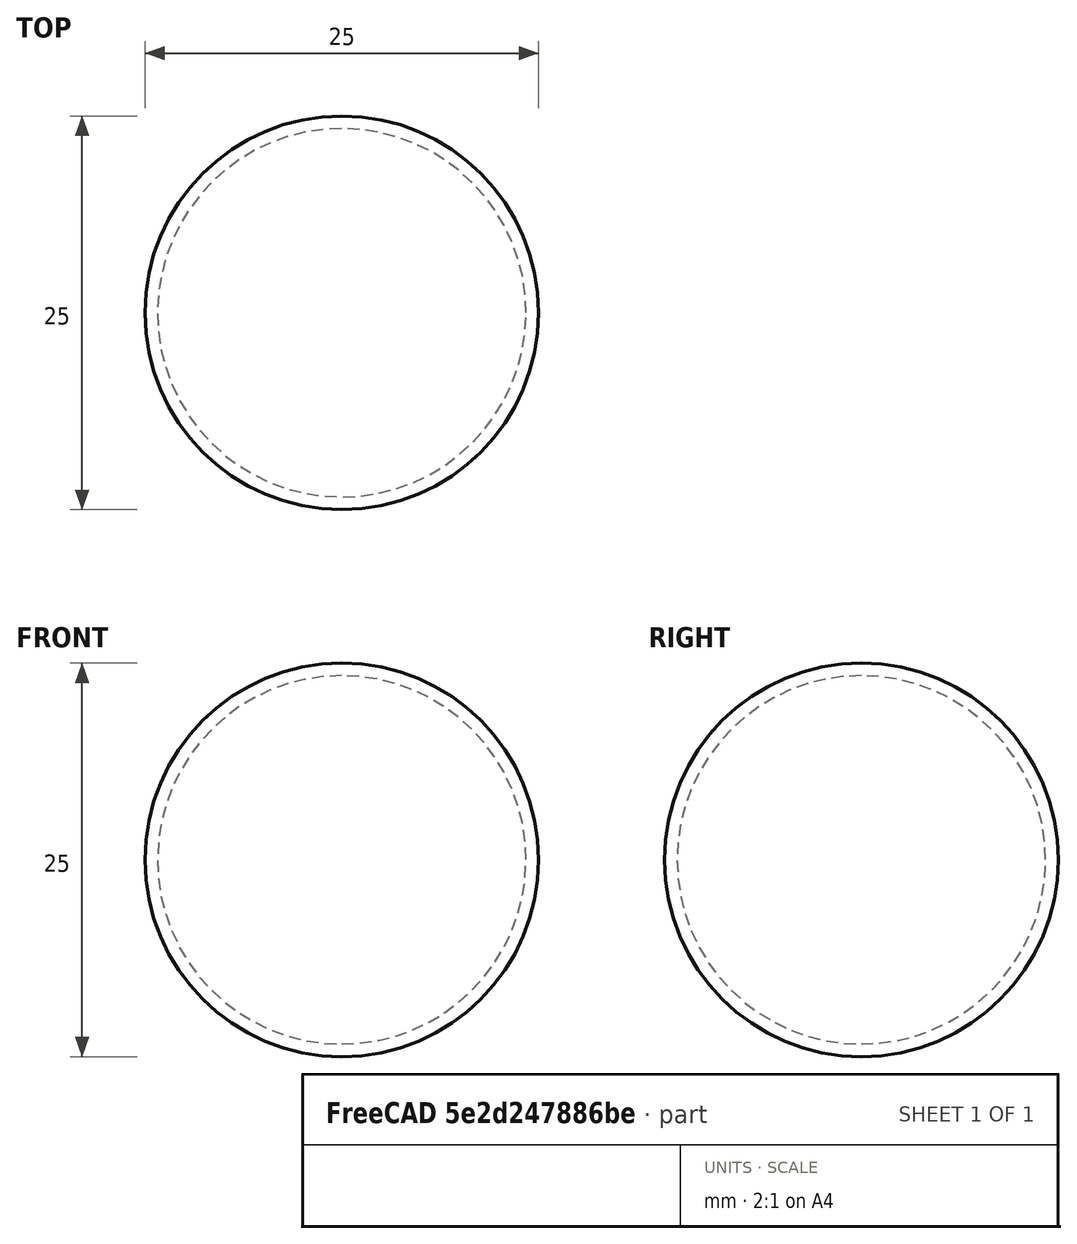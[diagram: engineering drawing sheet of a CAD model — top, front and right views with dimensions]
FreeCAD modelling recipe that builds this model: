
FCSTD DOCUMENT  (FreeCAD 2021.1015R24301 +3962 (Git))
Label: sphere
License: All rights reserved
LicenseURL: http://en.wikipedia.org/wiki/All_rights_reserved
objects: Sketcher::SketchObject×1, PartDesign::Revolution×1, PartDesign::Body×1, Mesh::Feature×1
note: 5 computed .brp shape members not serialized (recipe doc carries the construction recipe); baked Part::Feature solids carry a one-line shape summary decoded from their .brp

FEATURE [Sketcher::SketchObject] Sketch
  FullyConstrained = true
  MapMode = 5
  Placement = pos=(0,0,0) rot=(1,0,0;1.5708rad)
  Support = -> [XZ_Plane]
  sketch-geometry (4):
    g0: ArcOfCircle CenterX=0 CenterY=12.5 CenterZ=0 NormalX=0 NormalY=0 NormalZ=1 AngleXU=0 Radius=12.5 StartAngle=4.71239 EndAngle=7.85398
    g1: ArcOfCircle CenterX=0 CenterY=12.5 CenterZ=0 NormalX=0 NormalY=0 NormalZ=1 AngleXU=0 Radius=11.7 StartAngle=4.71239 EndAngle=7.85398
    g2: LineSegment StartX=-2.3e-15 StartY=0 StartZ=0 EndX=-2.3e-15 EndY=0.8 EndZ=0
    g3: LineSegment StartX=0 StartY=24.2 StartZ=0 EndX=0 EndY=25 EndZ=0
  constraints (12):
    c: PointOnObject(g0,g-2)
    c: Coincident(g0,g-1)
    c: PointOnObject(g0,g-2)
    c: Coincident(g1,g0)
    c: Coincident(g2,g0)
    c: Coincident(g2,g1)
    c: Coincident(g3,g1)
    c: Coincident(g3,g0)
    c: Vertical(g2)
    c: Vertical(g3)
    c: Diameter(g0) = 25
    c: DistanceY(g2,g2) = 0.8
FEATURE [PartDesign::Revolution] Revolution
  Angle = 360
  Axis = (0,2e-16,1)
  Base = (0,0,0)
  ClaimChildren = false
  Fit = 0
  FitJoin = 0
  InnerFit = 0
  InnerFitJoin = 0
  NewSolid = false
  Placement = pos=(0,0,0) rot=(1,0,0;1.5708rad)
  Profile = -> Sketch
  ReferenceAxis = -> Sketch [V_Axis]
  Reversed = true
  Suppress = false
  _ProfileBasedVersion = 1
FEATURE [PartDesign::Body] Body
  AutoGroupSolids = false
  ExportMode = 0
  Group = -> [Sketch,Revolution]
  Origin = -> Origin
  Tip = -> Revolution
  _ExportChildren = -> [Revolution]
  _GroupVersion = 1
FEATURE [Mesh::Feature] Mesh  label="sphere_20x0.8"
